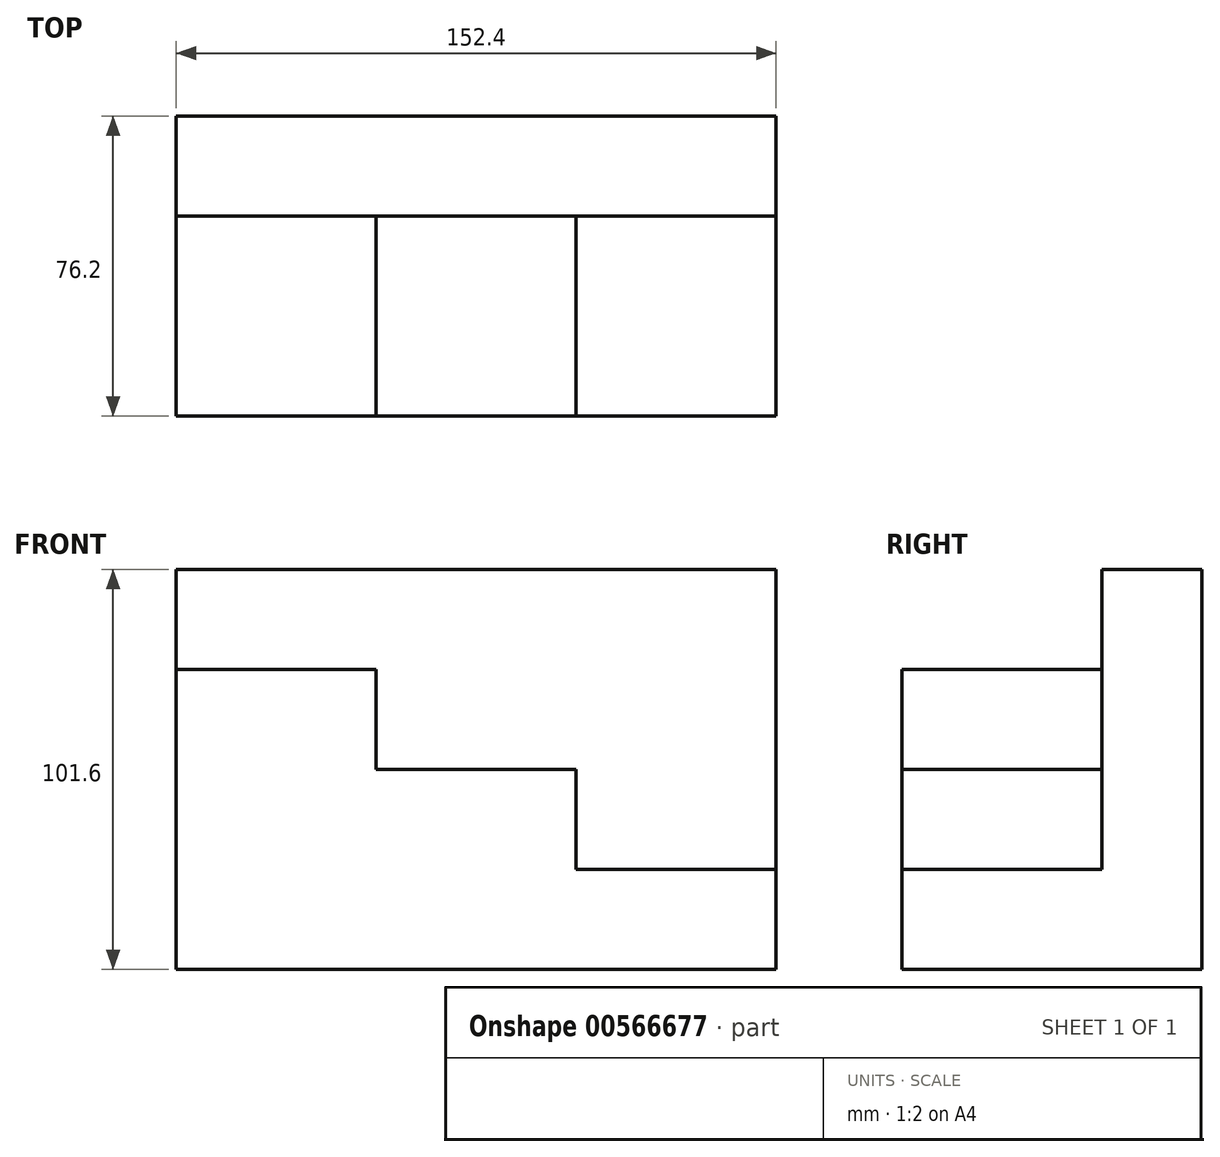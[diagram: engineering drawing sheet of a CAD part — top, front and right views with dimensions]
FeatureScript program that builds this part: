
annotation { "Feature Type Name" : "Feature", "Feature Type Description" : "" }
export const myFeature = defineFeature(function(context is Context, id is Id, definition is map)
    precondition{}
    {
        {
            var Q0;
            Q0=qCreatedBy(makeId("Top.planeOp"),FACE);
            var sketch = newSketch(context, id + "F0", { "sketchPlane" : qUnion([Q0])});
            skLineSegment(sketch, "E0.bottom", {"start": v(23.56, -122.87) * mm, "end": v(175.96, -122.87) * mm});
            skLineSegment(sketch, "E0.top", {"start": v(23.56, -199.07) * mm, "end": v(175.96, -199.07) * mm});
            skLineSegment(sketch, "E0.left", {"start": v(23.56, -122.87) * mm, "end": v(23.56, -199.07) * mm});
            skLineSegment(sketch, "E0.right", {"start": v(175.96, -122.87) * mm, "end": v(175.96, -199.07) * mm});
            skSolve(sketch);
        }
        {
            var Q0;
            Q0=makeQuery(id+"F0.imprint","IMPRINT",FACE,{"disambiguationData":[TD([[makeQuery(id+"F0.imprint","IMPRINT",EDGE,{"derivedFrom":sQuery(id+"F0.wireOp",EDGE,"E0.bottom")}),-1.0]])]});
            extrude(context, id + "F1", {"entities" : qUnion([Q0]), "depth" : 101.6 * mm, "offsetDistance" : 25.4 * mm});
        }
        {
            var Q0;
            Q0=makeQuery(id+"F1.opExtrude","SWEPT_FACE",FACE,{"disambiguationData":[OSD([sQuery(id+"F0.wireOp",EDGE,"E0.top")])]});
            var sketch = newSketch(context, id + "F2", { "sketchPlane" : qUnion([Q0])});
            skLineSegment(sketch, "E1.bottom", {"start": v(23.56, 76.2) * mm, "end": v(74.36, 76.2) * mm});
            skLineSegment(sketch, "E1.top", {"start": v(23.56, 0) * mm, "end": v(74.36, 0) * mm});
            skLineSegment(sketch, "E1.left", {"start": v(23.56, 76.2) * mm, "end": v(23.56, 0) * mm});
            skLineSegment(sketch, "E1.right", {"start": v(74.36, 76.2) * mm, "end": v(74.36, 0) * mm});
            skPoint(sketch, "E2.firstSnap0", {"position": v(23.56, 50.8) * mm});
            skLineSegment(sketch, "E2.bottom", {"start": v(74.36, 50.8) * mm, "end": v(125.16, 50.8) * mm});
            skLineSegment(sketch, "E2.top", {"start": v(74.36, 0) * mm, "end": v(125.16, 0) * mm});
            skLineSegment(sketch, "E2.left", {"start": v(74.36, 50.8) * mm, "end": v(74.36, 0) * mm});
            skLineSegment(sketch, "E2.right", {"start": v(125.16, 50.8) * mm, "end": v(125.16, 0) * mm});
            skLineSegment(sketch, "E3.bottom", {"start": v(125.16, 0) * mm, "end": v(175.96, 0) * mm});
            skLineSegment(sketch, "E3.top", {"start": v(125.16, 25.4) * mm, "end": v(175.96, 25.4) * mm});
            skLineSegment(sketch, "E3.left", {"start": v(125.16, 0) * mm, "end": v(125.16, 25.4) * mm});
            skLineSegment(sketch, "E3.right", {"start": v(175.96, 0) * mm, "end": v(175.96, 25.4) * mm});
            skSolve(sketch);
        }
        {
            var Q0;
            {var subQ2=sQuery(id+"F2.wireOp",EDGE,"E1.bottom");Q0=makeQuery(id+"F2.imprint","IMPRINT",FACE,{"disambiguationData":[TD([[makeQuery(id+"F2.imprint","IMPRINT",EDGE,{"derivedFrom":subQ2}),1.0]])]});}
            extrude(context, id + "F3", {"entities" : qUnion([Q0]), "operationType" : NewBodyOperationType.REMOVE, "oppositeDirection" : true, "depth" : 50.8 * mm, "offsetDistance" : 25.4 * mm});
        }
    });
